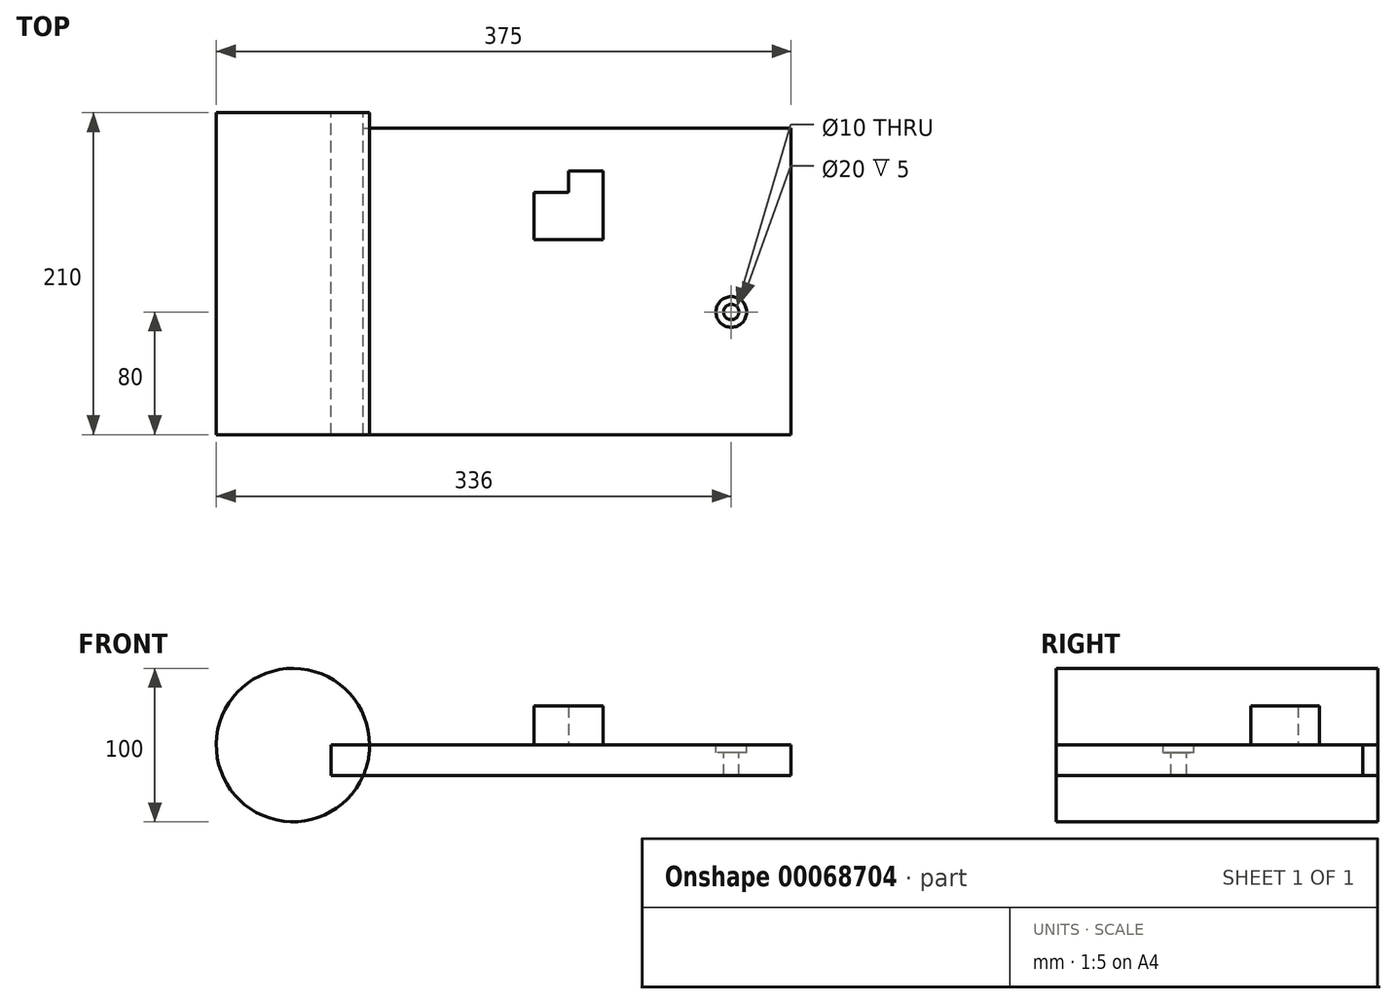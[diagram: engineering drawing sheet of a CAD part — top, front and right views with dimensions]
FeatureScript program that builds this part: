
annotation { "Feature Type Name" : "Feature", "Feature Type Description" : "" }
export const myFeature = defineFeature(function(context is Context, id is Id, definition is map)
    precondition{}
    {
        {
            var Q0;
            Q0=qCreatedBy(makeId("Front.planeOp"),FACE);
            var sketch = newSketch(context, id + "F0", { "sketchPlane" : qUnion([Q0])});
            skCircle(sketch, "E0", {"center": v(0, 0) * mm, "radius": 50 * mm});
            skLineSegment(sketch, "E1.bottom", {"start": v(25, 0) * mm, "end": v(325, 0) * mm});
            skLineSegment(sketch, "E1.top", {"start": v(25, -20) * mm, "end": v(325, -20) * mm});
            skLineSegment(sketch, "E1.left", {"start": v(25, 0) * mm, "end": v(25, -20) * mm});
            skLineSegment(sketch, "E1.right", {"start": v(325, 0) * mm, "end": v(325, -20) * mm});
            skSolve(sketch);
        }
        {
            var Q0;
            {var subQ5=sQuery(id+"F0.wireOp",EDGE,"E1.left");Q0=makeQuery(id+"F0.imprint","IMPRINT",FACE,{"disambiguationData":[TD([[makeQuery(id+"F0.imprint","IMPRINT",EDGE,{"derivedFrom":subQ5}),-1.0]])]});}
            var Q1;
            {var subQ5=sQuery(id+"F0.wireOp",EDGE,"E1.right");Q1=makeQuery(id+"F0.imprint","IMPRINT",FACE,{"disambiguationData":[TD([[makeQuery(id+"F0.imprint","IMPRINT",EDGE,{"derivedFrom":subQ5}),-1.0]])]});}
            extrude(context, id + "F1", {"entities" : qUnion([Q0, Q1]), "depth" : 200 * mm});
        }
        {
            var Q0;
            Q0=makeQuery(id+"F1.opExtrude","CAP_FACE",FACE,{"disambiguationData":[OSD([sQuery(id+"F0.wireOp",EDGE,"E0"),sQuery(id+"F0.wireOp",EDGE,"E1.bottom"),sQuery(id+"F0.wireOp",EDGE,"E1.top"),sQuery(id+"F0.wireOp",EDGE,"E1.left")])],"isStart":true});
            extrude(context, id + "F2", {"entities" : qUnion([Q0]), "operationType" : NewBodyOperationType.ADD, "depth" : 10 * mm});
        }
        {
            var Q0;
            {var subQ0=sQuery(id+"F0.wireOp",EDGE,"E1.bottom");Q0=makeQuery(id+"F1.opExtrude","SWEPT_FACE",FACE,{"disambiguationData":[OSD([subQ0]),TDD([makeQuery(id+"F0.imprint","IMPRINT",EDGE,{"disambiguationData":[TD([[makeQuery(id+"F0.imprint","INTERSECT",VERTEX,{"derivedFrom":[subQ0,sQuery(id+"F0.wireOp",EDGE,"E1.right")]}),1.0]])],"derivedFrom":subQ0})])]});}
            var sketch = newSketch(context, id + "F3", { "sketchPlane" : qUnion([Q0])});
            skPoint(sketch, "E2", {"position": v(286, -120) * mm});
            skSolve(sketch);
        }
        {
            var Q0;
            Q0=sQuery(id+"F3.wireOp",VERTEX,"E2");
            var Q1;
            Q1=makeQuery(id+"F1.opExtrude","SWEPT_BODY",BODY,{"disambiguationData":[OSD([sQuery(id+"F0.wireOp",EDGE,"E0"),sQuery(id+"F0.wireOp",EDGE,"E1.bottom"),sQuery(id+"F0.wireOp",EDGE,"E1.top"),sQuery(id+"F0.wireOp",EDGE,"E1.right")])]});
            hole(context, id + "F4", {"style" : HoleStyle.C_BORE, "holeDiameter" : 10 * mm, "cBoreDiameter" : 20 * mm, "cBoreDepth" : 5 * mm, "endStyle" : HoleEndStyle.THROUGH, "locations" : qUnion([Q0]), "scope" : qUnion([Q1])});
        }
        {
            var Q0;
            {var subQ0=sQuery(id+"F0.wireOp",EDGE,"E1.bottom");Q0=makeQuery(id+"F1.opExtrude","SWEPT_FACE",FACE,{"disambiguationData":[OSD([subQ0]),TDD([makeQuery(id+"F0.imprint","IMPRINT",EDGE,{"disambiguationData":[TD([[makeQuery(id+"F0.imprint","INTERSECT",VERTEX,{"derivedFrom":[subQ0,sQuery(id+"F0.wireOp",EDGE,"E1.right")]}),1.0]])],"derivedFrom":subQ0})])]});}
            var sketch = newSketch(context, id + "F5", { "sketchPlane" : qUnion([Q0])});
            skLineSegment(sketch, "E3.bottom", {"start": v(157.2, -72.82) * mm, "end": v(202.29, -72.82) * mm});
            skLineSegment(sketch, "E3.top", {"start": v(157.2, -42.15) * mm, "end": v(202.29, -42.15) * mm});
            skLineSegment(sketch, "E3.left", {"start": v(157.2, -72.82) * mm, "end": v(157.2, -42.15) * mm});
            skLineSegment(sketch, "E3.right", {"start": v(202.29, -72.82) * mm, "end": v(202.29, -42.15) * mm});
            skPoint(sketch, "E4.oppositeSnap0", {"position": v(179.75, -42.15) * mm});
            skLineSegment(sketch, "E4.bottom", {"start": v(202.29, -57.48) * mm, "end": v(179.75, -57.48) * mm});
            skLineSegment(sketch, "E4.top", {"start": v(202.29, -28.17) * mm, "end": v(179.75, -28.17) * mm});
            skLineSegment(sketch, "E4.left", {"start": v(202.29, -57.48) * mm, "end": v(202.29, -28.17) * mm});
            skLineSegment(sketch, "E4.right", {"start": v(179.75, -57.48) * mm, "end": v(179.75, -28.17) * mm});
            skSolve(sketch);
        }
        {
            var Q0;
            Q0=makeQuery(id+"F5.imprint","IMPRINT",FACE,{"disambiguationData":[TD([[makeQuery(id+"F5.imprint","IMPRINT",EDGE,{"derivedFrom":sQuery(id+"F5.wireOp",EDGE,"E3.bottom")}),1.0]])]});
            var Q1;
            {var subQ5=sQuery(id+"F5.wireOp",EDGE,"E4.bottom");Q1=makeQuery(id+"F5.imprint","IMPRINT",FACE,{"disambiguationData":[TD([[makeQuery(id+"F5.imprint","IMPRINT",EDGE,{"derivedFrom":subQ5}),-1.0]])]});}
            var Q2;
            {var subQ5=sQuery(id+"F5.wireOp",EDGE,"E4.top");Q2=makeQuery(id+"F5.imprint","IMPRINT",FACE,{"disambiguationData":[TD([[makeQuery(id+"F5.imprint","IMPRINT",EDGE,{"derivedFrom":subQ5}),1.0]])]});}
            extrude(context, id + "F6", {"entities" : qUnion([Q0, Q1, Q2]), "operationType" : NewBodyOperationType.ADD, "depth" : 25.4 * mm});
        }
    });
